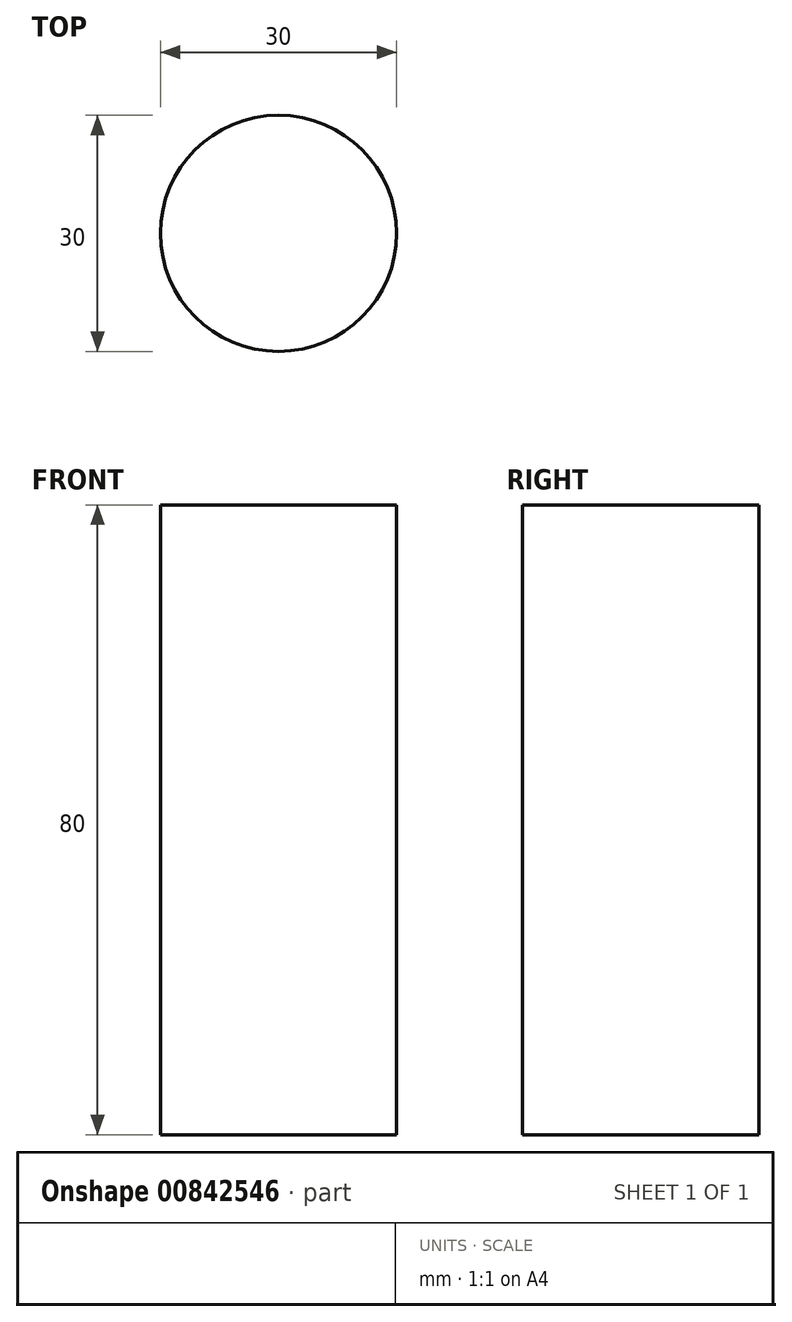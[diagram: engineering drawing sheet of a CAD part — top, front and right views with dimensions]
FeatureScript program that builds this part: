
annotation { "Feature Type Name" : "Feature", "Feature Type Description" : "" }
export const myFeature = defineFeature(function(context is Context, id is Id, definition is map)
    precondition{}
    {
        {
            var Q0;
            Q0=qCreatedBy(makeId("Top.planeOp"),FACE);
            var sketch = newSketch(context, id + "F0", { "sketchPlane" : qUnion([Q0])});
            skCircle(sketch, "E0", {"center": v(0, 0) * mm, "radius": 15 * mm});
            skSolve(sketch);
        }
        {
            var Q0;
            Q0 = qSketchRegion(id + "F0", true);
            extrude(context, id + "F1", {"entities" : qUnion([Q0]), "depth" : 80 * mm, "offsetDistance" : 25 * mm});
        }
    });
